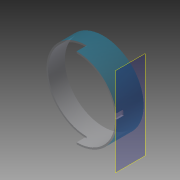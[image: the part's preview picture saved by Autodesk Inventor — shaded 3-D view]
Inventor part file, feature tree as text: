
AUTODESK INVENTOR PART (.ipt)
format: ipt  version: 2013 (Build 170138000, 138)  size: 110,080 bytes
history: native  units: in
note: dims shown in document units (in); Inventor stores cm internally (conversion verified against a paired STEP export)
features: extrude x3, sketch x3, plane x1
ambient origin geometry x8: Origin, YZ Plane, XZ Plane, XY Plane, X Axis, Y Axis, Z Axis, Center Point
bodies: Solid1 (feature_tree)
feature tree (7):
  extrude  "Extrusion1"  Depth=11.5in
  extrude  "Extrusion3"  Depth=1.5in TaperAngle=0.0deg
  plane  "Work Plane1"
  extrude  "Extrusion4"  Depth=0.75in
  sketch  "Sketch1"  dims[d0=12.0in d1=11.5in]
  sketch  "Sketch2"  dims[d2=4.0in d3=0.0in d6=1.5in d7=0.0in]
  sketch  "Sketch3"  dims[d8=1.0in d9=0.75in d10=0.1875in d11=4.0in d12=1.5in d13=0.0in]
